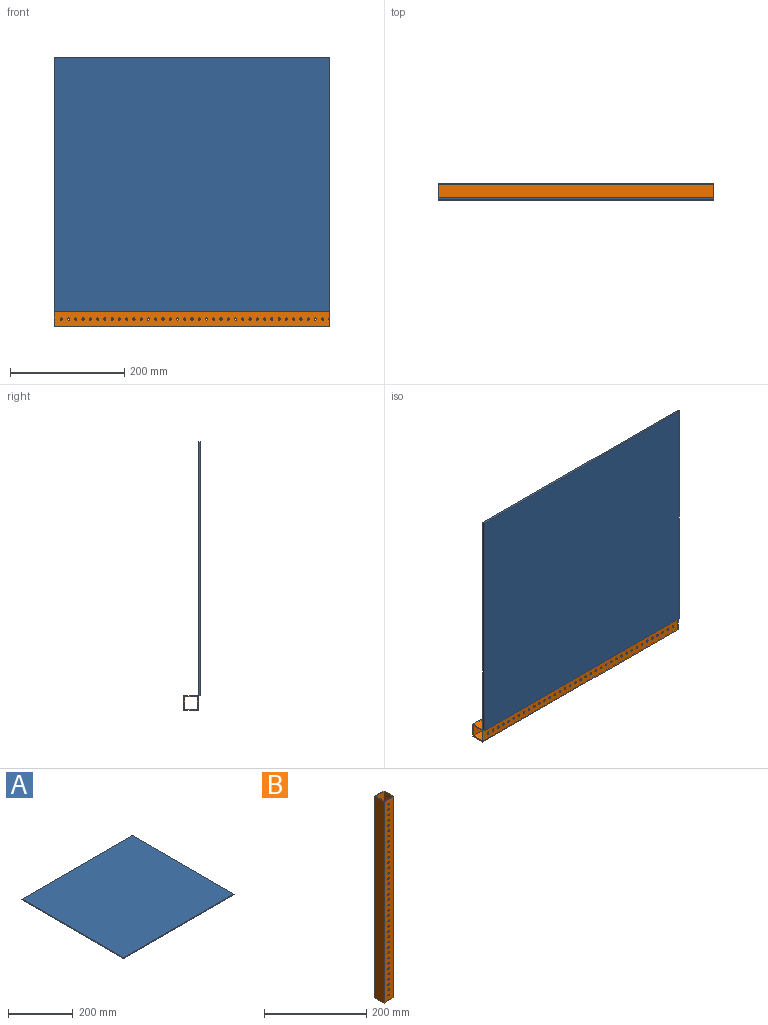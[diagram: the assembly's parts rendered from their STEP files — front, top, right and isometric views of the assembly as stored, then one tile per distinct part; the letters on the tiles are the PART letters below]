
ASSEMBLY  parts=2 mates=1
PART A: 6 faces, bbox 482.6x444.5x3.2 mm
  f0: plane 444.5x3.18mm, normal (-1,0,0), area 1411.3mm2, adj f1,f3,f4,f5
  f1: plane 482.6x3.18mm, normal (0,-1,0), area 1532.3mm2, adj f0,f2,f4,f5
  f2: plane 444.5x3.18mm, normal (1,0,0), area 1411.3mm2, adj f1,f3,f4,f5
  f3: plane 482.6x3.18mm, normal (0,1,0), area 1532.3mm2, adj f0,f2,f4,f5
  f4: plane 482.6x444.5mm, normal (0,0,1), area 214515.7mm2, adj f0,f1,f2,f3
  f5: plane 482.6x444.5mm, normal (0,0,-1), area 214515.7mm2, adj f0,f1,f2,f3
PART B: 87 faces, bbox 25.4x25.4x482.6 mm
  f0: plane 482.6x25.4mm, normal (0,-1,0), area 11830.5mm2, adj f1,f2,f3,f9,f10,f12,f50,f51
  f1: plane 25.4x10.8mm, normal (0,0,-1), area 69.6mm2, adj f0,f2,f4,f5,f6,f8,f11,f12
  f2: plane 482.6x25.4mm, normal (-1,0,0), area 12258mm2, adj f0,f1,f8,f9
  f3: plane 482.6x25.4mm, normal (1,0,0), area 12258mm2, adj f0,f8,f9,f10
  f4: plane 482.6x22.23mm, normal (0,1,0), area 10298.3mm2, adj f1,f5,f7,f9,f10,f12,f50,f51
  f5: plane 482.6x22.23mm, normal (1,0,0), area 10725.8mm2, adj f1,f4,f6,f9
  f6: plane 482.6x22.23mm, normal (0,-1,0), area 10298.3mm2, adj f1,f5,f7,f9,f10,f11,f13,f14
  f7: plane 482.6x22.23mm, normal (-1,0,0), area 10725.8mm2, adj f4,f6,f9,f10
  f8: plane 482.6x25.4mm, normal (0,1,0), area 11830.5mm2, adj f1,f2,f3,f9,f10,f11,f13,f14
  f9: plane 25.4x25.4mm, normal (0,0,1), area 151.2mm2, adj f0,f2,f3,f4,f5,f6,f7,f8
  f10: plane 25.4x10.8mm, normal (0,0,-1), area 69.6mm2, adj f0,f3,f4,f6,f7,f8,f11,f12
  f11: cylinder r=1.91mm len=3.81mm, axis (0,-1,0), area 9.5mm2, adj f1,f6,f8,f10
  f12: cylinder r=1.91mm len=3.81mm, axis (0,-1,0), area 9.5mm2, adj f0,f1,f4,f10
  f13: cylinder r=1.91mm len=3.81mm, axis (0,-1,0), area 19mm2, adj f6,f8
  f14: cylinder r=1.91mm len=3.81mm, axis (0,-1,0), area 19mm2, adj f6,f8
  f15: cylinder r=1.91mm len=3.81mm, axis (0,-1,0), area 19mm2, adj f6,f8
  f16: cylinder r=1.91mm len=3.81mm, axis (0,-1,0), area 19mm2, adj f6,f8
  f17: cylinder r=1.91mm len=3.81mm, axis (0,-1,0), area 19mm2, adj f6,f8
  f18: cylinder r=1.91mm len=3.81mm, axis (0,-1,0), area 19mm2, adj f6,f8
  f19: cylinder r=1.91mm len=3.81mm, axis (0,-1,0), area 19mm2, adj f6,f8
  f20: cylinder r=1.91mm len=3.81mm, axis (0,-1,0), area 19mm2, adj f6,f8
  f21: cylinder r=1.91mm len=3.81mm, axis (0,-1,0), area 19mm2, adj f6,f8
  f22: cylinder r=1.91mm len=3.81mm, axis (0,-1,0), area 19mm2, adj f6,f8
  f23: cylinder r=1.91mm len=3.81mm, axis (0,-1,0), area 19mm2, adj f6,f8
  f24: cylinder r=1.91mm len=3.81mm, axis (0,-1,0), area 19mm2, adj f6,f8
  f25: cylinder r=1.91mm len=3.81mm, axis (0,-1,0), area 19mm2, adj f6,f8
  f26: cylinder r=1.91mm len=3.81mm, axis (0,-1,0), area 19mm2, adj f6,f8
  f27: cylinder r=1.91mm len=3.81mm, axis (0,-1,0), area 19mm2, adj f6,f8
  f28: cylinder r=1.91mm len=3.81mm, axis (0,-1,0), area 19mm2, adj f6,f8
  f29: cylinder r=1.91mm len=3.81mm, axis (0,-1,0), area 19mm2, adj f6,f8
  f30: cylinder r=1.91mm len=3.81mm, axis (0,-1,0), area 19mm2, adj f6,f8
  f31: cylinder r=1.91mm len=3.81mm, axis (0,-1,0), area 19mm2, adj f6,f8
  f32: cylinder r=1.91mm len=3.81mm, axis (0,-1,0), area 19mm2, adj f6,f8
  f33: cylinder r=1.91mm len=3.81mm, axis (0,-1,0), area 19mm2, adj f6,f8
  f34: cylinder r=1.91mm len=3.81mm, axis (0,-1,0), area 19mm2, adj f6,f8
  f35: cylinder r=1.91mm len=3.81mm, axis (0,-1,0), area 19mm2, adj f6,f8
  f36: cylinder r=1.91mm len=3.81mm, axis (0,-1,0), area 19mm2, adj f6,f8
  f37: cylinder r=1.91mm len=3.81mm, axis (0,-1,0), area 19mm2, adj f6,f8
  f38: cylinder r=1.91mm len=3.81mm, axis (0,-1,0), area 19mm2, adj f6,f8
  f39: cylinder r=1.91mm len=3.81mm, axis (0,-1,0), area 19mm2, adj f6,f8
  f40: cylinder r=1.91mm len=3.81mm, axis (0,-1,0), area 19mm2, adj f6,f8
  f41: cylinder r=1.91mm len=3.81mm, axis (0,-1,0), area 19mm2, adj f6,f8
  f42: cylinder r=1.91mm len=3.81mm, axis (0,-1,0), area 19mm2, adj f6,f8
  f43: cylinder r=1.91mm len=3.81mm, axis (0,-1,0), area 19mm2, adj f6,f8
  f44: cylinder r=1.91mm len=3.81mm, axis (0,-1,0), area 19mm2, adj f6,f8
  f45: cylinder r=1.91mm len=3.81mm, axis (0,-1,0), area 19mm2, adj f6,f8
  f46: cylinder r=1.91mm len=3.81mm, axis (0,-1,0), area 19mm2, adj f6,f8
  f47: cylinder r=1.91mm len=3.81mm, axis (0,-1,0), area 19mm2, adj f6,f8
  f48: cylinder r=1.91mm len=3.81mm, axis (0,-1,0), area 19mm2, adj f6,f8
  f49: cylinder r=1.91mm len=3.81mm, axis (0,-1,0), area 19mm2, adj f6,f8
  f50: cylinder r=1.91mm len=3.81mm, axis (0,-1,0), area 19mm2, adj f0,f4
  f51: cylinder r=1.91mm len=3.81mm, axis (0,-1,0), area 19mm2, adj f0,f4
  f52: cylinder r=1.91mm len=3.81mm, axis (0,-1,0), area 19mm2, adj f0,f4
  f53: cylinder r=1.91mm len=3.81mm, axis (0,-1,0), area 19mm2, adj f0,f4
  f54: cylinder r=1.91mm len=3.81mm, axis (0,-1,0), area 19mm2, adj f0,f4
  f55: cylinder r=1.91mm len=3.81mm, axis (0,-1,0), area 19mm2, adj f0,f4
  f56: cylinder r=1.91mm len=3.81mm, axis (0,-1,0), area 19mm2, adj f0,f4
  f57: cylinder r=1.91mm len=3.81mm, axis (0,-1,0), area 19mm2, adj f0,f4
  f58: cylinder r=1.91mm len=3.81mm, axis (0,-1,0), area 19mm2, adj f0,f4
  f59: cylinder r=1.91mm len=3.81mm, axis (0,-1,0), area 19mm2, adj f0,f4
  f60: cylinder r=1.91mm len=3.81mm, axis (0,-1,0), area 19mm2, adj f0,f4
  f61: cylinder r=1.91mm len=3.81mm, axis (0,-1,0), area 19mm2, adj f0,f4
  f62: cylinder r=1.91mm len=3.81mm, axis (0,-1,0), area 19mm2, adj f0,f4
  f63: cylinder r=1.91mm len=3.81mm, axis (0,-1,0), area 19mm2, adj f0,f4
  f64: cylinder r=1.91mm len=3.81mm, axis (0,-1,0), area 19mm2, adj f0,f4
  f65: cylinder r=1.91mm len=3.81mm, axis (0,-1,0), area 19mm2, adj f0,f4
  f66: cylinder r=1.91mm len=3.81mm, axis (0,-1,0), area 19mm2, adj f0,f4
  f67: cylinder r=1.91mm len=3.81mm, axis (0,-1,0), area 19mm2, adj f0,f4
  f68: cylinder r=1.91mm len=3.81mm, axis (0,-1,0), area 19mm2, adj f0,f4
  f69: cylinder r=1.91mm len=3.81mm, axis (0,-1,0), area 19mm2, adj f0,f4
  f70: cylinder r=1.91mm len=3.81mm, axis (0,-1,0), area 19mm2, adj f0,f4
  f71: cylinder r=1.91mm len=3.81mm, axis (0,-1,0), area 19mm2, adj f0,f4
  f72: cylinder r=1.91mm len=3.81mm, axis (0,-1,0), area 19mm2, adj f0,f4
  f73: cylinder r=1.91mm len=3.81mm, axis (0,-1,0), area 19mm2, adj f0,f4
  f74: cylinder r=1.91mm len=3.81mm, axis (0,-1,0), area 19mm2, adj f0,f4
  f75: cylinder r=1.91mm len=3.81mm, axis (0,-1,0), area 19mm2, adj f0,f4
  f76: cylinder r=1.91mm len=3.81mm, axis (0,-1,0), area 19mm2, adj f0,f4
  f77: cylinder r=1.91mm len=3.81mm, axis (0,-1,0), area 19mm2, adj f0,f4
  f78: cylinder r=1.91mm len=3.81mm, axis (0,-1,0), area 19mm2, adj f0,f4
  f79: cylinder r=1.91mm len=3.81mm, axis (0,-1,0), area 19mm2, adj f0,f4
  f80: cylinder r=1.91mm len=3.81mm, axis (0,-1,0), area 19mm2, adj f0,f4
  f81: cylinder r=1.91mm len=3.81mm, axis (0,-1,0), area 19mm2, adj f0,f4
  f82: cylinder r=1.91mm len=3.81mm, axis (0,-1,0), area 19mm2, adj f0,f4
  f83: cylinder r=1.91mm len=3.81mm, axis (0,-1,0), area 19mm2, adj f0,f4
  f84: cylinder r=1.91mm len=3.81mm, axis (0,-1,0), area 19mm2, adj f0,f4
  f85: cylinder r=1.91mm len=3.81mm, axis (0,-1,0), area 19mm2, adj f0,f4
  f86: cylinder r=1.91mm len=3.81mm, axis (0,-1,0), area 19mm2, adj f0,f4
PLACE A rot(axis=(1,0,0),90deg) t=(-219.29,276.81,-83.71)mm
PLACE B rot(axis=(0,-1,0),90deg) t=(334.22,251.38,-182.35)mm
MATE fastened B.f0 <-> A.f5  axis (0,-1,0) through (-148.38,276.81,-223.28)mm
